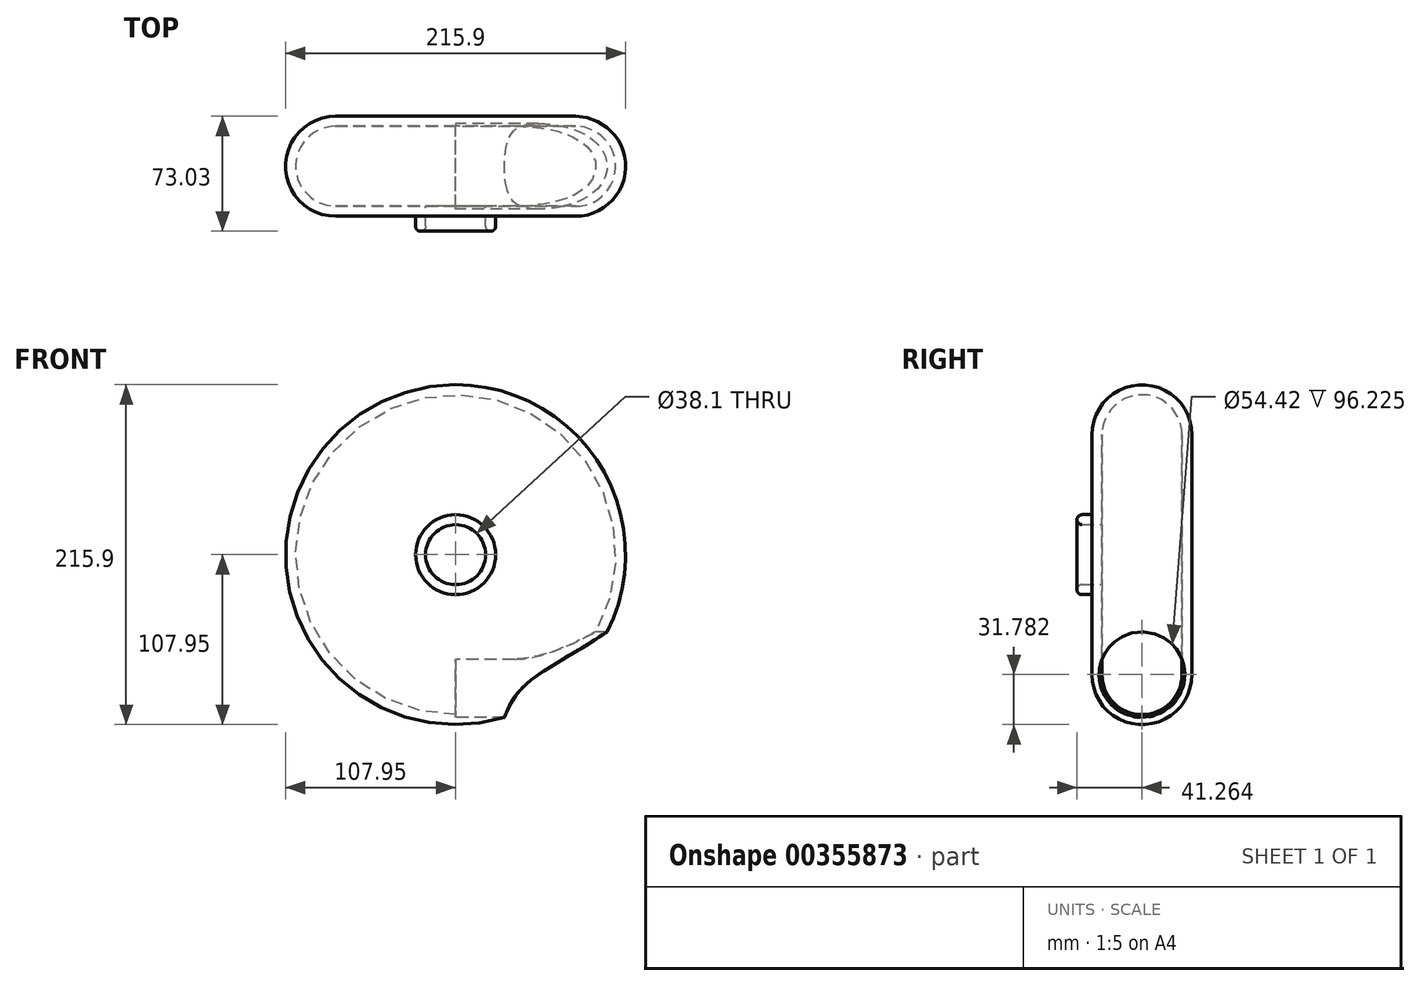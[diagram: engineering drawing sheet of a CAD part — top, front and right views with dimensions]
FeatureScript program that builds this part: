
annotation { "Feature Type Name" : "Feature", "Feature Type Description" : "" }
export const myFeature = defineFeature(function(context is Context, id is Id, definition is map)
    precondition{}
    {
        {
            var Q0;
            Q0=qCreatedBy(makeId("Top.planeOp"),FACE);
            var sketch = newSketch(context, id + "F0", { "sketchPlane" : qUnion([Q0])});
            skLineSegment(sketch, "E0", {"start": v(0, 0) * mm, "end": v(76.2, 0) * mm});
            skLineSegment(sketch, "E1", {"start": v(0, 0) * mm, "end": v(0, -6.35) * mm});
            skLineSegment(sketch, "E2", {"start": v(0, -6.35) * mm, "end": v(0, -57.15) * mm});
            skLineSegment(sketch, "E3", {"start": v(0, -57.15) * mm, "end": v(0, -63.5) * mm});
            skLineSegment(sketch, "E4", {"start": v(0, -63.5) * mm, "end": v(76.2, -63.5) * mm});
            skLineSegment(sketch, "E5", {"start": v(76.2, 0) * mm, "end": v(76.2, -63.5) * mm});
            skArc(sketch, "E6", {"start": v(76.2, -63.5) * mm, "mid": v(107.95, -31.75) * mm, "end": v(76.2, 0) * mm});
            skLineSegment(sketch, "E7", {"start": v(0, -6.35) * mm, "end": v(76.2, -6.35) * mm});
            skLineSegment(sketch, "E8", {"start": v(0, -57.15) * mm, "end": v(76.2, -57.15) * mm});
            skArc(sketch, "E9", {"start": v(76.2, -57.15) * mm, "mid": v(101.6, -31.75) * mm, "end": v(76.2, -6.35) * mm});
            skLineSegment(sketch, "E10", {"start": v(0, -63.5) * mm, "end": v(25.4, -63.5) * mm});
            skLineSegment(sketch, "E11", {"start": v(25.4, -63.5) * mm, "end": v(25.4, -69.85) * mm});
            skLineSegment(sketch, "E12", {"start": v(25.4, -63.5) * mm, "end": v(19.05, -63.5) * mm});
            skLineSegment(sketch, "E13", {"start": v(19.05, -63.5) * mm, "end": v(19.05, -69.85) * mm});
            skLineSegment(sketch, "E14", {"start": v(19.05, -69.85) * mm, "end": v(25.4, -69.85) * mm});
            skArc(sketch, "E15", {"start": v(25.4, -69.85) * mm, "mid": v(22.23, -73.02) * mm, "end": v(19.05, -69.85) * mm});
            skLineSegment(sketch, "E16", {"start": v(19.05, -63.5) * mm, "end": v(19.05, -57.15) * mm});
            skLineSegment(sketch, "E17", {"start": v(25.4, -69.85) * mm, "end": v(25.4, -76.2) * mm});
            skArc(sketch, "E18", {"start": v(19.05, -69.85) * mm, "mid": v(20.9, -74.34) * mm, "end": v(25.4, -76.2) * mm});
            skSolve(sketch);
        }
        {
            var Q0;
            {var subQ0=sQuery(id+"F0.wireOp",EDGE,"E0");Q0=makeQuery(id+"F0.imprint","IMPRINT",FACE,{"disambiguationData":[TD([[makeQuery(id+"F0.imprint","IMPRINT",EDGE,{"derivedFrom":subQ0}),-1.0]])]});}
            var Q1;
            {var subQ0=sQuery(id+"F0.wireOp",EDGE,"E6");Q1=makeQuery(id+"F0.imprint","IMPRINT",FACE,{"disambiguationData":[TD([[makeQuery(id+"F0.imprint","IMPRINT",EDGE,{"derivedFrom":subQ0}),1.0]])]});}
            var Q2;
            {var subQ4=sQuery(id+"F0.wireOp",EDGE,"E4");Q2=makeQuery(id+"F0.imprint","IMPRINT",FACE,{"disambiguationData":[TD([[makeQuery(id+"F0.imprint","IMPRINT",EDGE,{"derivedFrom":subQ4}),1.0]])]});}
            var Q3;
            Q3=makeQuery(id+"F0.imprint","IMPRINT",FACE,{"disambiguationData":[TD([[makeQuery(id+"F0.imprint","IMPRINT",EDGE,{"derivedFrom":sQuery(id+"F0.wireOp",EDGE,"E11")}),-1.0]])]});
            var Q4;
            Q4=makeQuery(id+"F0.imprint","IMPRINT",FACE,{"disambiguationData":[TD([[makeQuery(id+"F0.imprint","IMPRINT",EDGE,{"derivedFrom":sQuery(id+"F0.wireOp",EDGE,"E14")}),-1.0]])]});
            var Q5;
            Q5=makeQuery(id+"F0.imprint","IMPRINT",FACE,{"disambiguationData":[TD([[makeQuery(id+"F0.imprint","IMPRINT",EDGE,{"derivedFrom":sQuery(id+"F0.wireOp",EDGE,"E15")}),1.0]])]});
            var Q6;
            Q6=sQuery(id+"F0.wireOp",EDGE,"E2");
            revolve(context, id + "F1", {"entities" : qUnion([Q0, Q1, Q2, Q3, Q4, Q5]), "axis" : qUnion([Q6]), "revolveType" : RevolveType.FULL});
        }
        {
            var Q0;
            Q0=qCreatedBy(makeId("Right.planeOp"),FACE);
            var sketch = newSketch(context, id + "F2", { "sketchPlane" : qUnion([Q0])});
            skLineSegment(sketch, "E19", {"start": v(-76.44, -76.17) * mm, "end": v(0, -76.17) * mm});
            skLineSegment(sketch, "E20", {"start": v(0, -76.17) * mm, "end": v(-63.53, -76.17) * mm});
            skCircle(sketch, "E21", {"center": v(-31.77, -76.17) * mm, "radius": 27.2 * mm});
            skSolve(sketch);
        }
        {
            var Q0;
            Q0=qSketchRegion(id+"F2",true);
            extrude(context, id + "F3", {"entities" : qUnion([Q0]), "operationType" : NewBodyOperationType.REMOVE, "depth" : 101.6 * mm});
        }
    });
